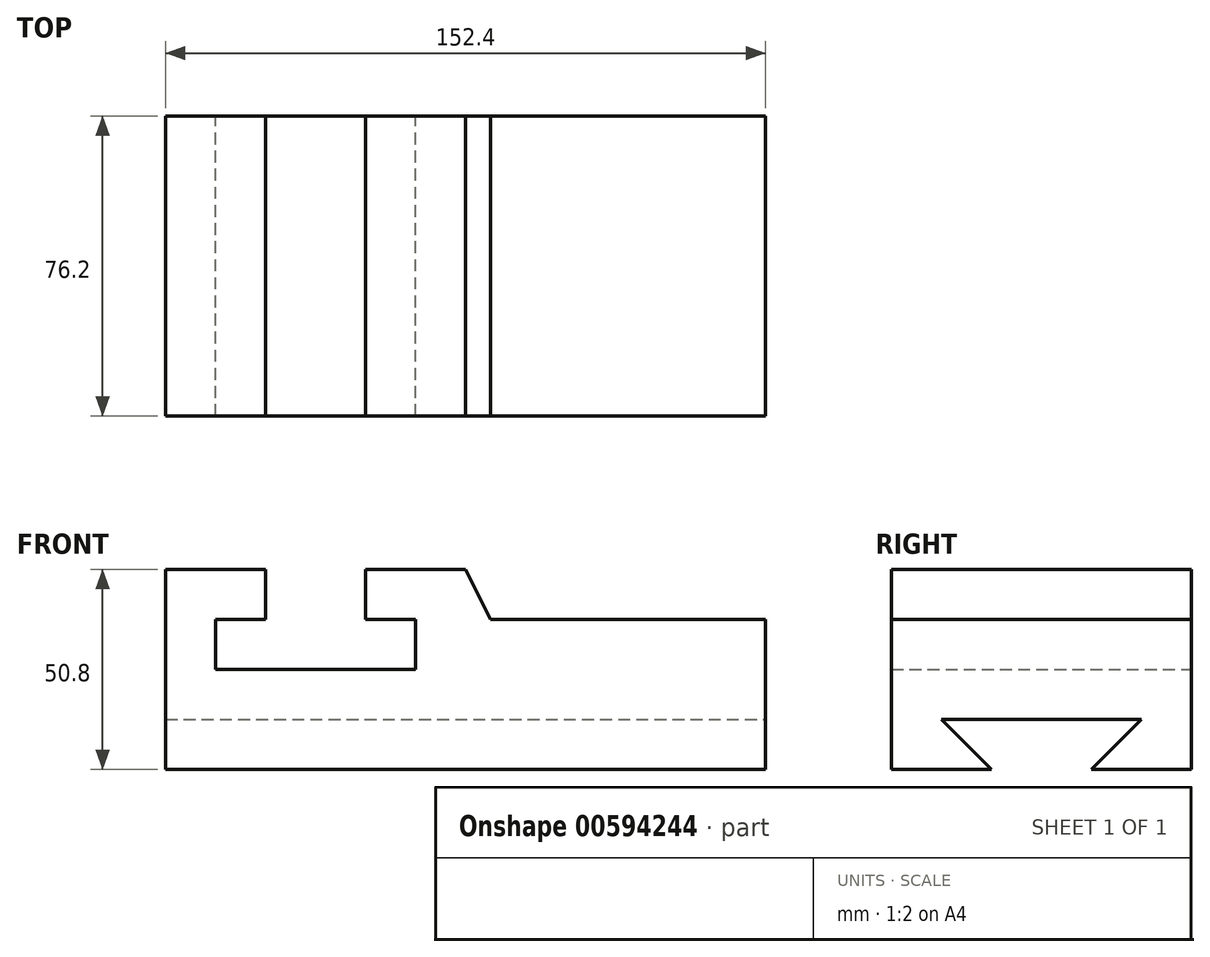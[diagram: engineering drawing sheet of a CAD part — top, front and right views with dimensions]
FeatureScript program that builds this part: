
annotation { "Feature Type Name" : "Feature", "Feature Type Description" : "" }
export const myFeature = defineFeature(function(context is Context, id is Id, definition is map)
    precondition{}
    {
        {
            var Q0;
            Q0=qCreatedBy(makeId("Front.planeOp"),FACE);
            var sketch = newSketch(context, id + "F0", { "sketchPlane" : qUnion([Q0])});
            skLineSegment(sketch, "E0", {"start": v(0, 0) * mm, "end": v(0, 50.8) * mm});
            skLineSegment(sketch, "E1", {"start": v(0, 50.8) * mm, "end": v(25.4, 50.8) * mm});
            skLineSegment(sketch, "E2", {"start": v(25.4, 50.8) * mm, "end": v(25.4, 38.1) * mm});
            skLineSegment(sketch, "E3", {"start": v(25.4, 38.1) * mm, "end": v(12.7, 38.1) * mm});
            skLineSegment(sketch, "E4", {"start": v(12.7, 38.1) * mm, "end": v(12.7, 25.4) * mm});
            skLineSegment(sketch, "E5", {"start": v(12.7, 25.4) * mm, "end": v(63.5, 25.4) * mm});
            skLineSegment(sketch, "E6", {"start": v(63.5, 25.4) * mm, "end": v(63.5, 38.1) * mm});
            skLineSegment(sketch, "E7", {"start": v(63.5, 38.1) * mm, "end": v(50.8, 38.1) * mm});
            skLineSegment(sketch, "E8", {"start": v(50.8, 38.1) * mm, "end": v(50.8, 50.8) * mm});
            skLineSegment(sketch, "E9", {"start": v(50.8, 50.8) * mm, "end": v(76.2, 50.8) * mm});
            skLineSegment(sketch, "E10", {"start": v(76.2, 50.8) * mm, "end": v(82.55, 38.1) * mm});
            skLineSegment(sketch, "E11", {"start": v(82.55, 38.1) * mm, "end": v(152.4, 38.1) * mm});
            skLineSegment(sketch, "E12", {"start": v(152.4, 38.1) * mm, "end": v(152.4, 0) * mm});
            skLineSegment(sketch, "E13", {"start": v(152.4, 0) * mm, "end": v(0, 0) * mm});
            skSolve(sketch);
        }
        {
            var Q0;
            Q0=makeQuery(id+"F0.imprint","IMPRINT",FACE,{"disambiguationData":[TD([[makeQuery(id+"F0.imprint","IMPRINT",EDGE,{"derivedFrom":sQuery(id+"F0.wireOp",EDGE,"E0")}),-1.0]])]});
            extrude(context, id + "F1", {"entities" : qUnion([Q0]), "depth" : 76.2 * mm, "offsetDistance" : 25.4 * mm});
        }
        {
            var Q0;
            Q0=makeQuery(id+"F1.opExtrude","SWEPT_FACE",FACE,{"disambiguationData":[OSD([sQuery(id+"F0.wireOp",EDGE,"E12")])]});
            var sketch = newSketch(context, id + "F2", { "sketchPlane" : qUnion([Q0])});
            skLineSegment(sketch, "E14", {"start": v(-76.2, 0) * mm, "end": v(-50.79, 0) * mm});
            skLineSegment(sketch, "E15", {"start": v(0, 0) * mm, "end": v(-25.4, 0) * mm});
            skLineSegment(sketch, "E16", {"start": v(-50.79, 0) * mm, "end": v(-63.5, 12.7) * mm});
            skLineSegment(sketch, "E17", {"start": v(-63.5, 12.7) * mm, "end": v(-12.7, 12.7) * mm});
            skLineSegment(sketch, "E18", {"start": v(-12.7, 12.7) * mm, "end": v(-25.4, 0) * mm});
            skSolve(sketch);
        }
        {
            var Q0;
            {var subQ0=sQuery(id+"F2.wireOp",EDGE,"E16");Q0=makeQuery(id+"F2.imprint","IMPRINT",FACE,{"disambiguationData":[TD([[makeQuery(id+"F2.imprint","IMPRINT",EDGE,{"derivedFrom":subQ0}),-1.0]])]});}
            extrude(context, id + "F3", {"entities" : qUnion([Q0]), "operationType" : NewBodyOperationType.REMOVE, "oppositeDirection" : true, "depth" : 152.4 * mm, "offsetDistance" : 25.4 * mm});
        }
    });
